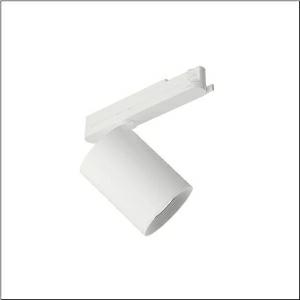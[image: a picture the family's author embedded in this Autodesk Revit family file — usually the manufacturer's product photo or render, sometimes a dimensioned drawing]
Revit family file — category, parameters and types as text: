
# Revit family: spot_11_51sd14mbb5a
name_source: partatom
category: Lighting Fixtures
units: mm (PartAtom-declared; Revit-internal decimal feet)

## family parameters
Cut with Voids When Loaded = No
Host = Face
Light Source = No
Part Type = Normal
Room Calculation Point = No
Round Connector Dimension = Use Diameter
Shared = No

## types (1)
- --- (1 x LED, 7340 lm, 50.2 W, 3000K)
    Apparent Load = 50 VA
    CIE Flux Codes = 95 98 100 100 100
    Color Rendering = 90
    Color Temperature = 3000K
    Default Elevation = 1800 mm
    Description = Spot 11, directional spotlight, light control with lens, of PMMA, LED rated luminous flux: 5.630lm, light colour: 930, control gear: ECG Multilumen, with 3-phase adapter, mains connection: 220..240V, AC, 50/60Hz, of aluminium, traffic white (RAL 9016), length: 213mm, diameter: 105mm, protection rating (complete): IP20, insulation class (complete): insulation class I (protective earthing), certification: CE, impact resistance: IK02, permissible ambient temperature for indoor applications: -20..+40°C, packaging unit: 1 piece
    Height = 175 mm
    Lamp = 1 x LED
    Lamp Light Flux = 7340 lm
    Lamp Power = 50.2 W
    Lamp count = 1
    Length = 105 mm
    Luminous efficacy = 146 lm/W
    Manufacturer = Siteco
    ModVariant = No
    Model = 51SD14MBB5A
    Mounting Place = Ceiling
    Mounting Type = Pendant
    Number of Poles = 1
    OnlyDefault = Yes
    Power Factor = 1
    Product Name = Spot 11
    Product group = directional spotlight
    ProductGroupID = 905
    Protection Class = Protection class I
    Protection Degree = IP 20
    RLX_Detail_Level = 1
    RLX_Emergency_Light_Flux = 0 lm
    RLX_Emergency_Type = 0
    RLX_Emergency_Type_DB = No
    RlxData = <blob elided: 17661 chars, md5=e3e44710>
    Socket = socket
    Standby Power = 0 W
    System Light Flux = 7340 lm
    System Power = 50 W
    Type Comments = factory setting: luminous flux: 100 % | (ON | ON | ON | ON) | 1050 mA
    Type Image = l_1006697.jpg
    URL = http://relux.com
    VarID = @adj_168915
    Voltage = 0 V
    Weight = 0.00 kg
    Width = 0 mm  [stored 0 ft]

note: [stored X ft] marks values corroborated as IEEE doubles in the binary element streams (Revit-internal decimal feet)

## geometry (parser evidence)
native form markers: Blend x4, Sweep x10
no freeform markers — native parametric forms only
